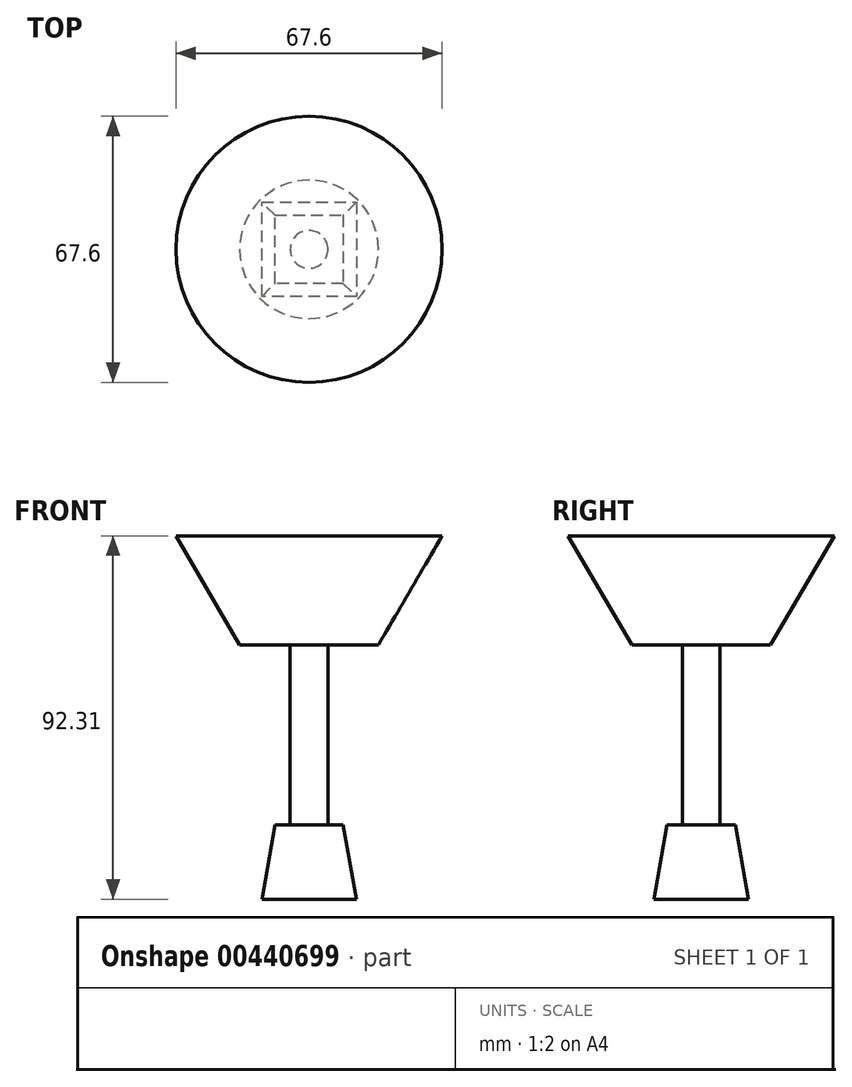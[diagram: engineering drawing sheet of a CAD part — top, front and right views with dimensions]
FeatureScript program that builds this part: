
annotation { "Feature Type Name" : "Feature", "Feature Type Description" : "" }
export const myFeature = defineFeature(function(context is Context, id is Id, definition is map)
    precondition{}
    {
        {
            var Q0;
            Q0=qCreatedBy(makeId("Top.planeOp"),FACE);
            var sketch = newSketch(context, id + "F0", { "sketchPlane" : qUnion([Q0])});
            skLineSegment(sketch, "E0.bottom", {"start": v(12, 12) * mm, "end": v(-12, 12) * mm});
            skLineSegment(sketch, "E0.top", {"start": v(12, -12) * mm, "end": v(-12, -12) * mm});
            skLineSegment(sketch, "E0.left", {"start": v(12, 12) * mm, "end": v(12, -12) * mm});
            skLineSegment(sketch, "E0.right", {"start": v(-12, 12) * mm, "end": v(-12, -12) * mm});
            skPoint(sketch, "E0.middle", {"position": v(0, 0) * mm});
            skSolve(sketch);
        }
        {
            var Q0;
            Q0 = qSketchRegion(id + "F0", true);
            extrude(context, id + "F1", {"entities" : qUnion([Q0]), "depth" : 18.9 * mm, "hasDraft" : true, "draftAngle" : 10 * degree, "draftPullDirection" : true});
        }
        {
            var Q0;
            Q0=makeQuery(id+"F1.opExtrude","CAP_FACE",FACE,{"disambiguationData":[OSD([sQuery(id+"F0.wireOp",EDGE,"E0.bottom"),sQuery(id+"F0.wireOp",EDGE,"E0.top"),sQuery(id+"F0.wireOp",EDGE,"E0.left"),sQuery(id+"F0.wireOp",EDGE,"E0.right")])],"isStart":false});
            var sketch = newSketch(context, id + "F2", { "sketchPlane" : qUnion([Q0])});
            skCircle(sketch, "E1", {"center": v(0, 0) * mm, "radius": 4.8 * mm});
            skSolve(sketch);
        }
        {
            var Q0;
            Q0 = qSketchRegion(id + "F2", true);
            extrude(context, id + "F3", {"entities" : qUnion([Q0]), "operationType" : NewBodyOperationType.ADD, "depth" : 45.7 * mm});
        }
        {
            var Q0;
            Q0=qCreatedBy(makeId("Front.planeOp"),FACE);
            var sketch = newSketch(context, id + "F4", { "sketchPlane" : qUnion([Q0])});
            skLineSegment(sketch, "E2", {"start": v(0, 64.6) * mm, "end": v(17.6, 64.6) * mm});
            skLineSegment(sketch, "E3", {"start": v(17.6, 64.6) * mm, "end": v(33.8, 92.31) * mm});
            skLineSegment(sketch, "E4", {"start": v(33.8, 92.31) * mm, "end": v(0, 92.31) * mm});
            skLineSegment(sketch, "E5", {"start": v(0, 92.31) * mm, "end": v(0, 64.6) * mm});
            skSolve(sketch);
        }
        {
            var Q0;
            Q0=makeQuery(id+"F4.imprint","IMPRINT",FACE,{"disambiguationData":[TD([[makeQuery(id+"F4.imprint","IMPRINT",EDGE,{"derivedFrom":sQuery(id+"F4.wireOp",EDGE,"E2")}),1.0]])]});
            var Q1;
            Q1 = qConstructionFilter(qBodyType(qCreatedBy(id + "F4" ,EDGE), BodyType.WIRE), ConstructionObject.NO);
            var Q2;
            Q2=sQuery(id+"F4.wireOp",EDGE,"E5");
            revolve(context, id + "F5", {"operationType" : NewBodyOperationType.ADD, "entities" : qUnion([Q0]), "surfaceEntities" : qUnion([Q1]), "axis" : qUnion([Q2]), "revolveType" : RevolveType.FULL});
        }
    });
